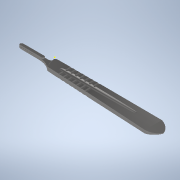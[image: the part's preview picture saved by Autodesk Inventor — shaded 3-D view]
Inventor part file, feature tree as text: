
AUTODESK INVENTOR PART (.ipt)
format: ipt  version: 2021 (Build 250183000, 183)  size: 434,688 bytes
history: native  units: mm
features: sketch x10, fillet x8, extrude x7, projected_geometry x3, mirror x2, plane x2, chamfer x2, revolve x1
ambient origin geometry x8: Origin, YZ Plane, XZ Plane, XY Plane, X Axis, Y Axis, Z Axis, Center Point
bodies: Solid1 (feature_tree)
feature tree (35):
  extrude  "Extrusion1"  Depth=8.5mm
  extrude  "Extrusion2"  Depth=13.0mm
  mirror  "Mirror1"
  plane  "Work Plane1"
  revolve  "Revolution2"  [1 undecoded]
  mirror  "Mirror2"
  fillet  "Fillet1"  Radius=10.5mm
  fillet  "Fillet4"  Radius=10.5mm
  extrude  "Extrusion4"  Depth=37.0mm
  extrude  "Extrusion5"  Depth=0.25mm
  extrude  "Extrusion7"  Depth=5.0mm
  chamfer  "Chamfer1"  Distance=1.4mm
  chamfer  "Chamfer2"  Distance=100.0mm
  extrude  "Extrusion6"  Depth=0.25mm
  fillet  "Fillet5"  [1 undecoded]
  fillet  "Fillet6"  Radius=315.75mm
  fillet  "Fillet7"  Radius=13.0mm
  fillet  "Fillet8"  Radius=2.0mm
  fillet  "Fillet9"  Radius=0.2mm
  plane  "Work Plane2"
  extrude  "Extrusion8"  Depth=10.0mm
  fillet  "Fillet10"  Radius=3.9mm
  sketch  "Sketch12"  dims[d23=8.5mm]
  sketch  "Sketch13"  dims[d24=0.3mm]
  sketch  "Sketch14"  dims[d29=10.0mm d30=1.4mm d31=100.0mm d32=4.5mm d33=90.0deg d34=315.75mm d37=13.0mm d38=2.0mm d39=0.2mm d40=70.0mm d42=3.5mm d43=10.0mm d45=10.0mm d47=3.9mm d48=0.0mm d59=23.0mm d60=2.5mm d61=2.0mm d62=10.0mm d64=1.35mm d65=1.4006mm d66=0.0mm d67=0.0mm d69=1.05mm d70=0.0mm d71=1.5mm d72=5.0mm d74=5.5mm d75=1.25mm d76=1.0mm d77=0.5mm d78=1.0mm d79=1.05mm d80=0.0mm d81=0.25mm d82=2.0mm d83=45.0deg d84=0.25mm d85=2.0mm d86=45.0deg d87=30.75mm d88=0.5mm d89=0.5mm d90=11.5mm d91=0.0mm d92=0.25mm]
  sketch  "Sketch3"  dims[d0=82.0mm d1=8.5mm]
  projected_geometry  "Projected Loop1"
  sketch  "Sketch5"  dims[d3=9.0mm d4=13.0mm]
  projected_geometry  "Projected Loop2"
  sketch  "Sketch6"  dims[d5=7.0mm d6=8.0mm d7=10.5mm d8=10.5mm]
  sketch  "Sketch7"  dims[d9=3.0mm d10=0.0mm d11=37.0mm]
  sketch  "Sketch8"  dims[d12=1.2mm d13=0.25mm]
  projected_geometry  "Projected Loop3"
  sketch  "Sketch9"  dims[d14=2.8mm d15=0.0mm d21=5.0mm]
  sketch  "Sketch10"  dims[d22=60.0mm]
note: 2 required parameter values undecoded (feature->parameter linkage not recoverable at this tier; creation-order binding heuristic only, values carry confidence <= 0.55)